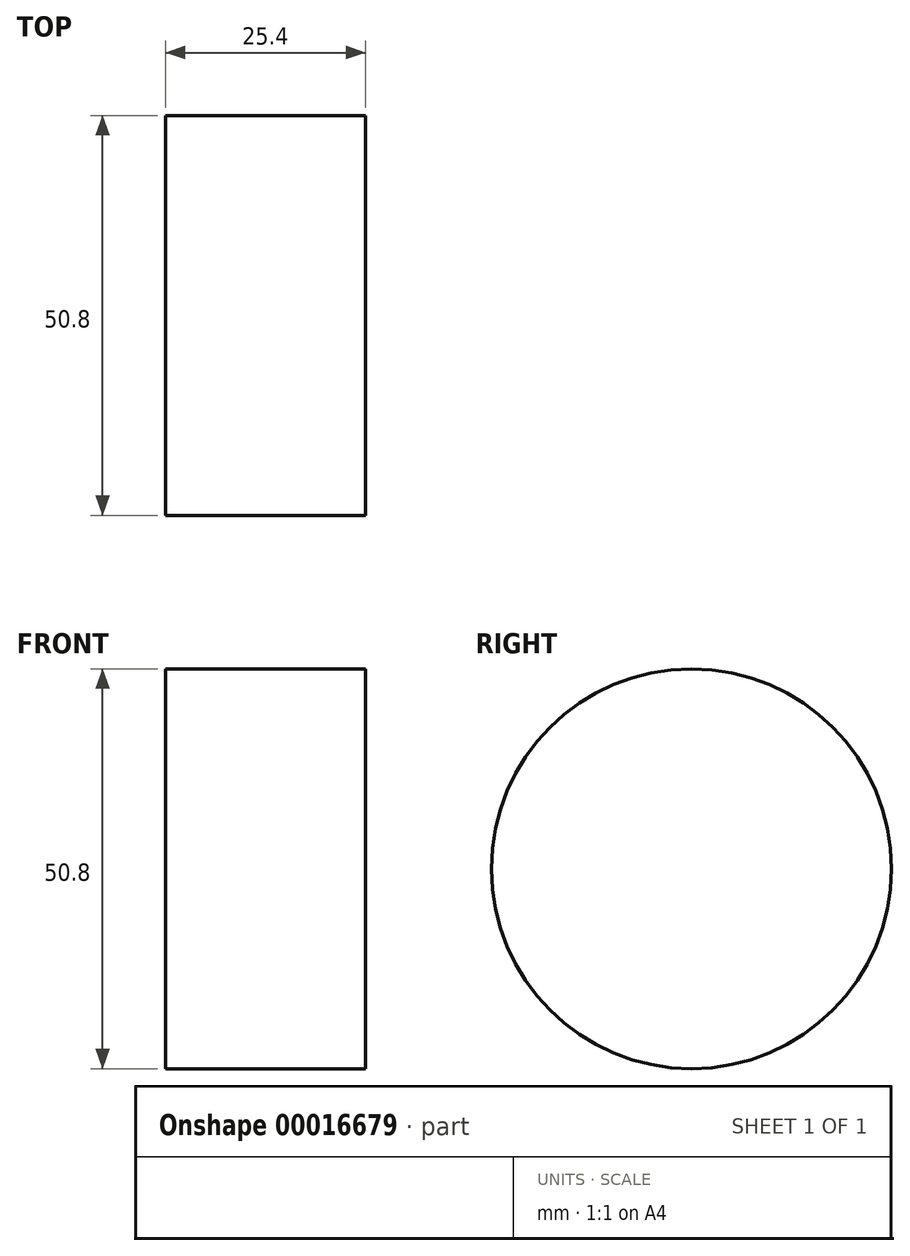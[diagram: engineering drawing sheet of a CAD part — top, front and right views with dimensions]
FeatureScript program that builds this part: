
annotation { "Feature Type Name" : "Feature", "Feature Type Description" : "" }
export const myFeature = defineFeature(function(context is Context, id is Id, definition is map)
    precondition{}
    {
        {
            var Q0;
            Q0=qCreatedBy(makeId("Right.planeOp"),FACE);
            var sketch = newSketch(context, id + "F0", { "sketchPlane" : qUnion([Q0])});
            skCircle(sketch, "E0", {"center": v(-37.94, -9.44) * mm, "radius": 25.4 * mm});
            skSolve(sketch);
        }
        {
            var Q0;
            Q0=makeQuery(id+"F0.imprint","IMPRINT",FACE,{"disambiguationData":[TD([[makeQuery(id+"F0.imprint","IMPRINT",EDGE,{"derivedFrom":sQuery(id+"F0.wireOp",EDGE,"E0")}),1.0]])]});
            extrude(context, id + "F1", {"entities" : qUnion([Q0]), "depth" : 25.4 * mm});
        }
    });
